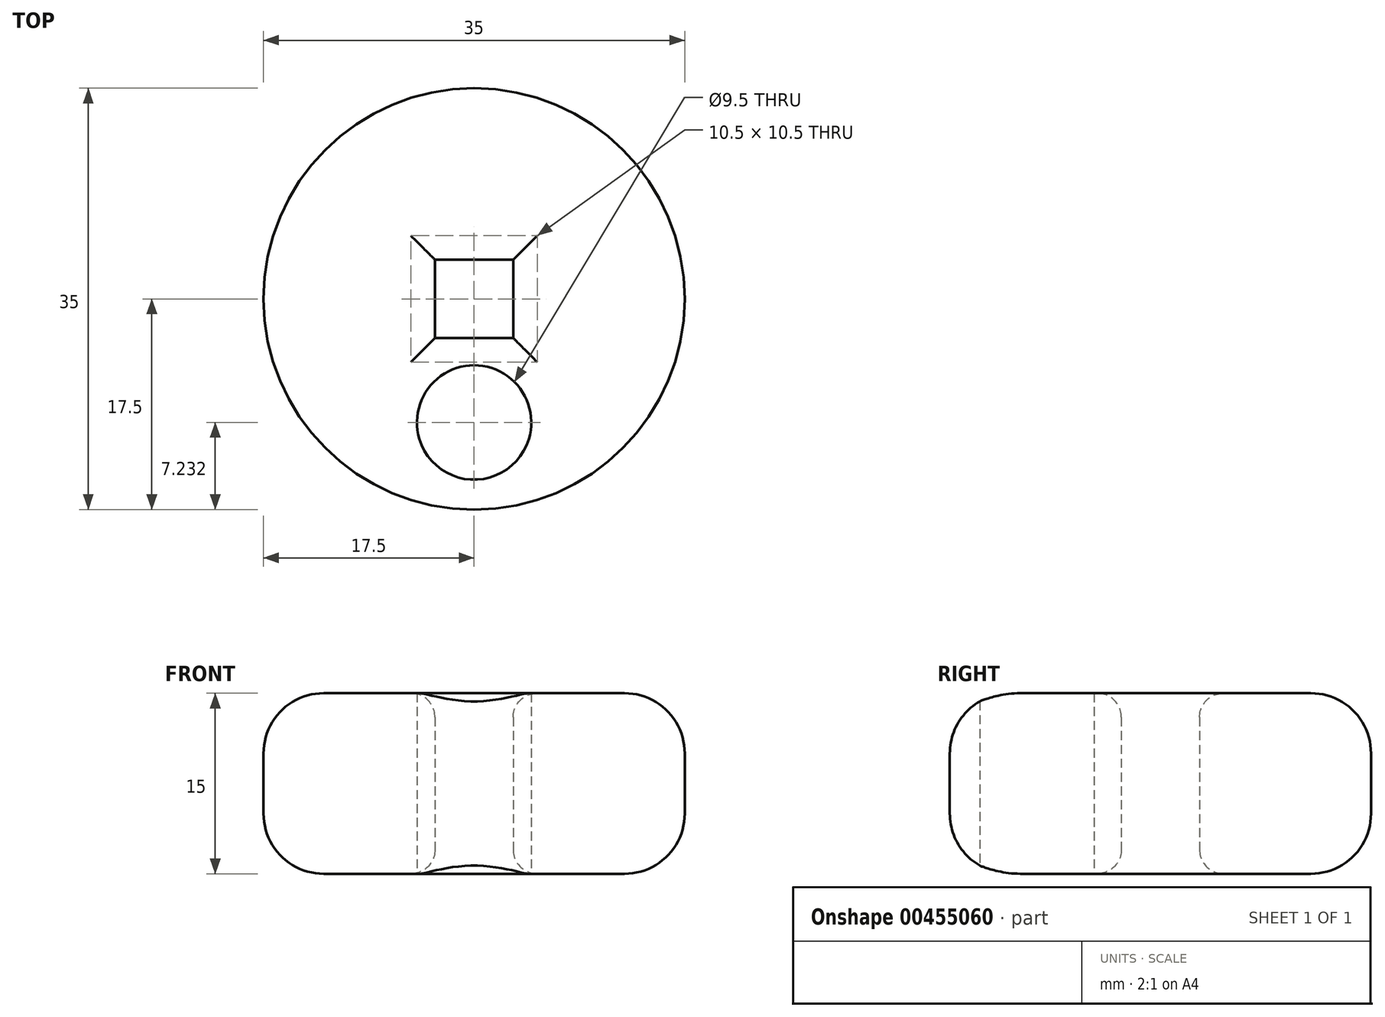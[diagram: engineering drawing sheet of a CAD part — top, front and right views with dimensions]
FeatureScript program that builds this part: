
annotation { "Feature Type Name" : "Feature", "Feature Type Description" : "" }
export const myFeature = defineFeature(function(context is Context, id is Id, definition is map)
    precondition{}
    {
        {
            var Q0;
            Q0=qCreatedBy(makeId("Top.planeOp"),FACE);
            var sketch = newSketch(context, id + "F0", { "sketchPlane" : qUnion([Q0])});
            skCircle(sketch, "E0", {"center": v(0, 0) * mm, "radius": 17.5 * mm});
            skCircle(sketch, "E1", {"center": v(0, -10.27) * mm, "radius": 4.75 * mm});
            skLineSegment(sketch, "E2.bottom", {"start": v(3.25, -3.25) * mm, "end": v(-3.25, -3.25) * mm});
            skLineSegment(sketch, "E2.top", {"start": v(3.25, 3.25) * mm, "end": v(-3.25, 3.25) * mm});
            skLineSegment(sketch, "E2.left", {"start": v(3.25, -3.25) * mm, "end": v(3.25, 3.25) * mm});
            skLineSegment(sketch, "E2.right", {"start": v(-3.25, -3.25) * mm, "end": v(-3.25, 3.25) * mm});
            skSolve(sketch);
        }
        {
            var Q0;
            Q0=makeQuery(id+"F0.imprint","IMPRINT",FACE,{"disambiguationData":[TD([[makeQuery(id+"F0.imprint","IMPRINT",EDGE,{"derivedFrom":sQuery(id+"F0.wireOp",EDGE,"E0")}),1.0]])]});
            extrude(context, id + "F1", {"entities" : qUnion([Q0]), "depth" : 15 * mm});
        }
        {
            var Q0;
            Q0=makeQuery(id+"F1.opExtrude","CAP_EDGE",EDGE,{"disambiguationData":[OSD([sQuery(id+"F0.wireOp",EDGE,"E0")])],"isStart":false});
            var Q1;
            Q1=makeQuery(id+"F1.opExtrude","CAP_EDGE",EDGE,{"disambiguationData":[OSD([sQuery(id+"F0.wireOp",EDGE,"E0")])],"isStart":true});
            fillet(context, id + "F2", {"entities" : qUnion([Q0, Q1]), "radius" : 5 * mm, "tangentPropagation" : true, "allowEdgeOverflow" : false});
        }
        {
            var Q0;
            Q0=makeQuery(id+"F1.opExtrude","CAP_EDGE",EDGE,{"disambiguationData":[OSD([sQuery(id+"F0.wireOp",EDGE,"aFgaoz9V-Ca7q-axmY-a975-9k1QYWRIUf0o")])],"isStart":false});
            var Q1;
            Q1=makeQuery(id+"F1.opExtrude","CAP_EDGE",EDGE,{"disambiguationData":[OSD([sQuery(id+"F0.wireOp",EDGE,"aFgaoz9V-Ca7q-axmY-a975-9k1QYWRIUf0o")])],"isStart":true});
            var Q2;
            Q2=makeQuery(id+"F1.opExtrude","CAP_EDGE",EDGE,{"disambiguationData":[OSD([sQuery(id+"F0.wireOp",EDGE,"E2.right")])],"isStart":false});
            var Q3;
            Q3=makeQuery(id+"F1.opExtrude","CAP_EDGE",EDGE,{"disambiguationData":[OSD([sQuery(id+"F0.wireOp",EDGE,"E2.bottom")])],"isStart":false});
            var Q4;
            Q4=makeQuery(id+"F1.opExtrude","CAP_EDGE",EDGE,{"disambiguationData":[OSD([sQuery(id+"F0.wireOp",EDGE,"E2.top")])],"isStart":false});
            var Q5;
            Q5=makeQuery(id+"F1.opExtrude","CAP_EDGE",EDGE,{"disambiguationData":[OSD([sQuery(id+"F0.wireOp",EDGE,"E2.left")])],"isStart":false});
            var Q6;
            Q6=makeQuery(id+"F1.opExtrude","CAP_EDGE",EDGE,{"disambiguationData":[OSD([sQuery(id+"F0.wireOp",EDGE,"E2.right")])],"isStart":true});
            var Q7;
            Q7=makeQuery(id+"F1.opExtrude","CAP_EDGE",EDGE,{"disambiguationData":[OSD([sQuery(id+"F0.wireOp",EDGE,"E2.bottom")])],"isStart":true});
            var Q8;
            Q8=makeQuery(id+"F1.opExtrude","CAP_EDGE",EDGE,{"disambiguationData":[OSD([sQuery(id+"F0.wireOp",EDGE,"E2.left")])],"isStart":true});
            var Q9;
            Q9=makeQuery(id+"F1.opExtrude","CAP_EDGE",EDGE,{"disambiguationData":[OSD([sQuery(id+"F0.wireOp",EDGE,"E2.top")])],"isStart":true});
            fillet(context, id + "F3", {"entities" : qUnion([Q0, Q1, Q2, Q3, Q4, Q5, Q6, Q7, Q8, Q9]), "radius" : 2 * mm, "tangentPropagation" : true, "allowEdgeOverflow" : false});
        }
    });
